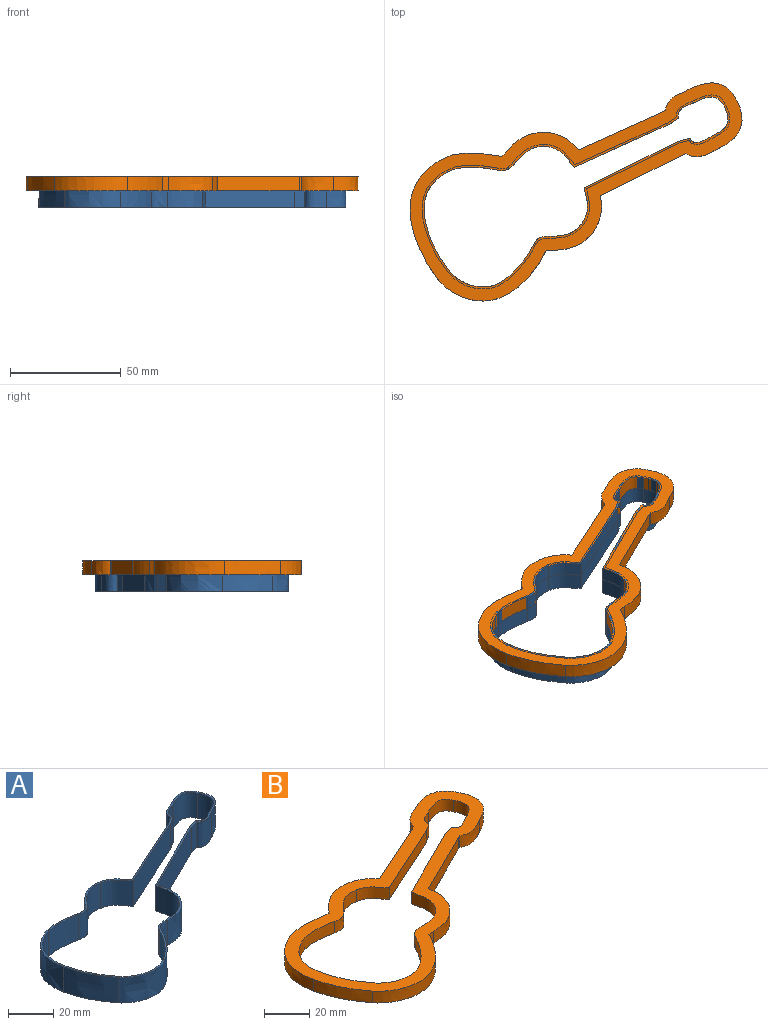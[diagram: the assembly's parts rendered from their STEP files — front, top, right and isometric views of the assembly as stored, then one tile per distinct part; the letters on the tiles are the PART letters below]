
ASSEMBLY  parts=2 mates=1
PART A: 40 faces, bbox 148.1x95.3x21.1 mm
  f0: plane 148.13x95.32mm, normal (0,0,1), area 329.4mm2, adj f2,f3,f4,f5,f6,f7,f8,f9
  f1: plane 148.13x95.32mm, normal (0,0,-1), area 329.4mm2, adj f2,f3,f4,f5,f6,f7,f8,f9
  f2: extruded ~25.13x15.15mm, area 442.4mm2, adj f0,f1,f3,f20
  f3: extruded ~22.81x13.72mm, area 351.5mm2, adj f0,f1,f2,f4
  f4: extruded ~25.65x13.72mm, area 391.4mm2, adj f0,f1,f3,f5
  f5: extruded ~16.68x13.83mm, area 300.6mm2, adj f0,f1,f4,f6
  f6: extruded ~13.72x7.24mm, area 115.2mm2, adj f0,f1,f5,f7
  f7: extruded ~15.64x13.72mm, area 254.5mm2, adj f0,f1,f6,f8
  f8: extruded ~14.36x13.72mm, area 201.9mm2, adj f0,f1,f7,f9
  f9: plane 41.77x20.68mm, normal (0.44,-0.9,0), area 639.2mm2, adj f0,f1,f8,f10
  f10: plane 13.72x4.44mm, normal (0.27,-0.96,0), area 63.2mm2, adj f0,f1,f9,f11
  f11: extruded ~13.72x10.03mm, area 154.3mm2, adj f0,f1,f10,f12
  f12: extruded ~15x13.72mm, area 268.2mm2, adj f0,f1,f11,f13
  f13: extruded ~15.6x13.72mm, area 251.1mm2, adj f0,f1,f12,f14
  f14: extruded ~13.72x6.92mm, area 144.1mm2, adj f0,f1,f13,f15
  f15: extruded ~13.72x3.79mm, area 62.7mm2, adj f0,f1,f14,f16
  f16: plane 42.24x19.08mm, normal (-0.41,0.91,0), area 635.7mm2, adj f0,f1,f15,f17
  f17: extruded ~13.72x11.6mm, area 207.3mm2, adj f0,f1,f16,f18
  f18: extruded ~14.55x13.72mm, area 225.3mm2, adj f0,f1,f17,f19
  f19: extruded ~13.72x9.08mm, area 151.7mm2, adj f0,f1,f18,f20
  f20: extruded ~18.64x13.72mm, area 257.6mm2, adj f0,f1,f2,f19
  f21: extruded ~24.08x14.49mm, area 423.9mm2, adj f0,f1,f22,f39
  f22: extruded ~22.45x13.72mm, area 345.9mm2, adj f0,f1,f21,f23
  f23: extruded ~24.45x13.72mm, area 373mm2, adj f0,f1,f22,f24
  f24: extruded ~16.33x13.72mm, area 294.1mm2, adj f0,f1,f23,f25
  f25: extruded ~13.72x7.97mm, area 127.8mm2, adj f0,f1,f24,f26
  f26: extruded ~14.93x13.72mm, area 242mm2, adj f0,f1,f25,f27
  f27: extruded ~14.44x13.72mm, area 203.1mm2, adj f0,f1,f26,f28
  f28: plane 42.48x21.03mm, normal (-0.44,0.9,0), area 650.2mm2, adj f0,f1,f27,f29
  f29: plane 13.72x5.15mm, normal (-0.27,0.96,0), area 73.4mm2, adj f0,f1,f28,f30
  f30: extruded ~13.72x9.17mm, area 144.3mm2, adj f0,f1,f29,f31
  f31: extruded ~13.84x13.72mm, area 250.2mm2, adj f0,f1,f30,f32
  f32: extruded ~14.38x13.72mm, area 231.6mm2, adj f0,f1,f31,f33
  f33: extruded ~13.72x6.59mm, area 137.3mm2, adj f0,f1,f32,f34
  f34: extruded ~13.72x4.31mm, area 71.1mm2, adj f0,f1,f33,f35
  f35: plane 42.88x19.37mm, normal (0.41,-0.91,0), area 645.4mm2, adj f0,f1,f34,f36
  f36: extruded ~13.72x11.49mm, area 207.6mm2, adj f0,f1,f35,f37
  f37: extruded ~13.81x13.72mm, area 214.2mm2, adj f0,f1,f36,f38
  f38: extruded ~13.72x9.88mm, area 163.6mm2, adj f0,f1,f37,f39
  f39: extruded ~18.24x13.72mm, area 252mm2, adj f0,f1,f21,f38
PART B: 41 faces, bbox 153.1x101.6x9.3 mm
  f0: plane 153.12x101.63mm, normal (0,0,1), area 2450.8mm2, adj f2,f3,f4,f5,f6,f7,f8,f9
  f1: plane 153.12x101.63mm, normal (0,0,-1), area 2450.8mm2, adj f2,f3,f4,f5,f6,f7,f8,f9
  f2: extruded ~6.35x3.29mm, area 27.8mm2, adj f0,f1,f19,f20
  f3: extruded ~31.58x19.16mm, area 257.5mm2, adj f0,f1,f4,f21
  f4: extruded ~25.04x12.24mm, area 178.5mm2, adj f0,f1,f3,f5
  f5: extruded ~33.02x9.44mm, area 233mm2, adj f0,f1,f4,f6
  f6: extruded ~18.59x15.55mm, area 155.6mm2, adj f0,f1,f5,f7
  f7: extruded ~6.35x2.86mm, area 18.2mm2, adj f0,f1,f6,f8
  f8: extruded ~20.14x10.93mm, area 154.1mm2, adj f0,f1,f7,f9
  f9: extruded ~13.77x6.35mm, area 89.6mm2, adj f0,f1,f8,f10
  f10: plane 37.51x18.57mm, normal (0.44,-0.9,0), area 265.7mm2, adj f0,f1,f9,f11
  f11: plane 6.35x1.13mm, normal (0.27,-0.96,0), area 7.4mm2, adj f0,f1,f10,f12
  f12: extruded ~14.25x6.35mm, area 96.6mm2, adj f0,f1,f11,f13
  f13: extruded ~22.09x11.16mm, area 175.9mm2, adj f0,f1,f12,f14
  f14: extruded ~23.05x7.8mm, area 171.5mm2, adj f0,f1,f13,f15
  f15: extruded ~9.3x8.67mm, area 84.5mm2, adj f0,f1,f14,f16
  f16: extruded ~6.35x1.18mm, area 9mm2, adj f0,f1,f15,f17
  f17: plane 38.02x17.18mm, normal (-0.41,0.91,0), area 264.9mm2, adj f0,f1,f16,f18
  f18: extruded ~12.53x7.67mm, area 95.3mm2, adj f0,f1,f17,f19
  f19: extruded ~19.13x7.57mm, area 136.2mm2, adj f0,f1,f2,f18
  f20: extruded ~6.35x1.27mm, area 8.1mm2, adj f0,f1,f2,f21
  f21: extruded ~21.13x6.35mm, area 134.9mm2, adj f0,f1,f3,f20
  f22: extruded ~24.08x14.49mm, area 196.2mm2, adj f0,f1,f23,f40
  f23: extruded ~22.45x11.02mm, area 160.1mm2, adj f0,f1,f22,f24
  f24: extruded ~24.45x7.03mm, area 172.7mm2, adj f0,f1,f23,f25
  f25: extruded ~16.33x13.53mm, area 136.2mm2, adj f0,f1,f24,f26
  f26: extruded ~7.97x6.35mm, area 59.2mm2, adj f0,f1,f25,f27
  f27: extruded ~14.93x7.4mm, area 112.1mm2, adj f0,f1,f26,f28
  f28: extruded ~14.44x6.35mm, area 94mm2, adj f0,f1,f27,f29
  f29: plane 42.48x21.03mm, normal (-0.44,0.9,0), area 301mm2, adj f0,f1,f28,f30
  f30: plane 6.35x5.15mm, normal (-0.27,0.96,0), area 34mm2, adj f0,f1,f29,f31
  f31: extruded ~9.17x6.35mm, area 66.8mm2, adj f0,f1,f30,f32
  f32: extruded ~13.84x8.14mm, area 115.8mm2, adj f0,f1,f31,f33
  f33: extruded ~14.38x6.35mm, area 107.2mm2, adj f0,f1,f32,f34
  f34: extruded ~6.59x6.35mm, area 63.6mm2, adj f0,f1,f33,f35
  f35: extruded ~6.35x4.31mm, area 32.9mm2, adj f0,f1,f34,f36
  f36: plane 42.88x19.37mm, normal (0.41,-0.91,0), area 298.8mm2, adj f0,f1,f35,f37
  f37: extruded ~11.49x9.17mm, area 96.1mm2, adj f0,f1,f36,f38
  f38: extruded ~13.81x6.35mm, area 99.2mm2, adj f0,f1,f37,f39
  f39: extruded ~9.88x6.35mm, area 75.8mm2, adj f0,f1,f38,f40
  f40: extruded ~18.24x6.35mm, area 116.7mm2, adj f0,f1,f22,f39
PLACE A t=(160.8,-9.12,-7.37)mm
PLACE B at identity
MATE fastened A.f0 <-> B.f0  axis (0,0,1) through (134.39,9.46,6.35)mm
